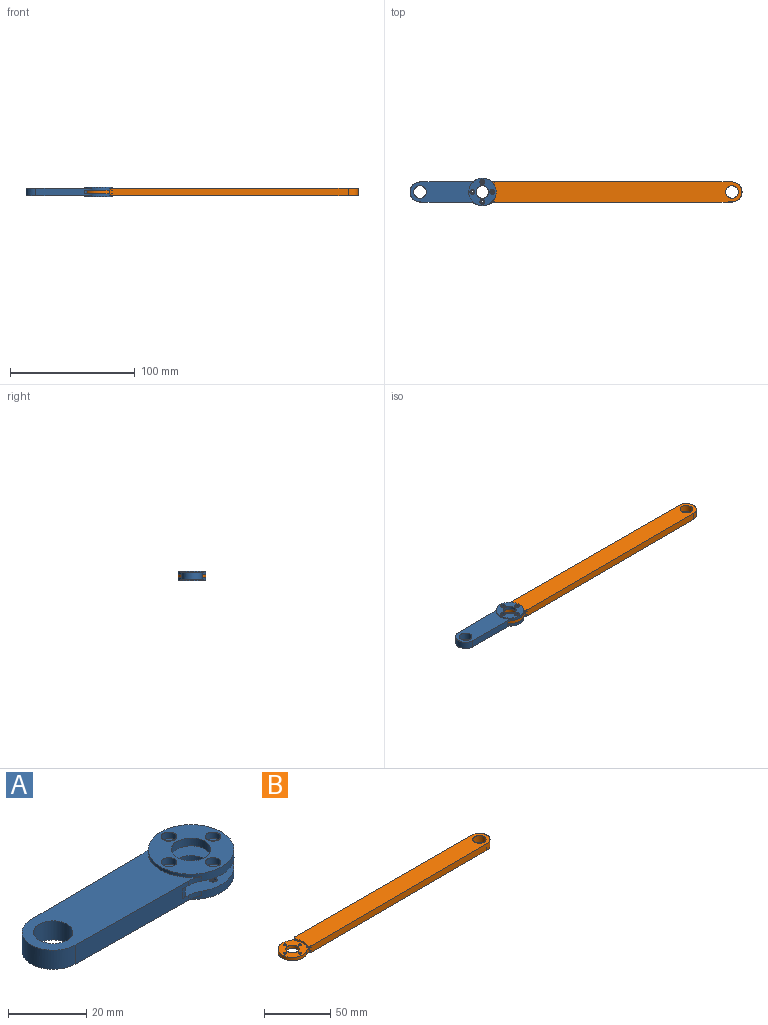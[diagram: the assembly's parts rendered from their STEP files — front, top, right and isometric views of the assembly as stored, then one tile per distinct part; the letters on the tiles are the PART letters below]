
ASSEMBLY  parts=2 mates=1
PART A: 65 faces, bbox 69x22.1x8 mm
  f0: cylinder r=2mm len=4mm, axis (0,0,1), area 25.1mm2, adj f8,f12
  f1: cylinder r=2mm len=4mm, axis (0,0,1), area 25.1mm2, adj f9,f12
  f2: cylinder r=2mm len=4mm, axis (0,0,1), area 25.1mm2, adj f10,f12
  f3: cylinder r=2mm len=4mm, axis (0,0,1), area 25.1mm2, adj f11,f12
  f4: plane 4.62x4mm, normal (0,0,-1), area 10.7mm2, adj f19,f20,f21,f22,f23,f24,f38
  f5: plane 4.62x4mm, normal (0,0,-1), area 10.7mm2, adj f13,f14,f15,f16,f17,f18,f39
  f6: plane 4.62x4mm, normal (0,0,-1), area 10.7mm2, adj f25,f26,f27,f28,f29,f30,f40
  f7: plane 4.62x4mm, normal (0,0,-1), area 10.7mm2, adj f31,f32,f33,f34,f35,f36,f41
  f8: plane 4.02x4mm, normal (0,0,1), area 9.4mm2, adj f0,f43
  f9: plane 4.02x4mm, normal (0,0,1), area 9.4mm2, adj f1,f44
  f10: plane 4.02x4mm, normal (0,0,1), area 9.4mm2, adj f2,f45
  f11: plane 4.02x4mm, normal (0,0,1), area 9.4mm2, adj f3,f46
  f12: plane 22.06x22mm, normal (0,0,1), area 249.7mm2, adj f0,f1,f2,f3,f42,f48
  f13: plane 2.31x1.7mm, normal (0,-1,0), area 3.9mm2, adj f5,f14,f18,f51
  f14: plane 2x1.7mm, normal (-0.87,-0.5,0), area 3.9mm2, adj f5,f13,f15,f51
  f15: plane 2x1.7mm, normal (-0.87,0.5,0), area 3.9mm2, adj f5,f14,f16,f51
  f16: plane 2.31x1.7mm, normal (0,1,0), area 3.9mm2, adj f5,f15,f17,f51
  f17: plane 2x1.7mm, normal (0.87,0.5,0), area 3.9mm2, adj f5,f16,f18,f51
  f18: plane 2x1.7mm, normal (0.87,-0.5,0), area 3.9mm2, adj f5,f13,f17,f51
  f19: plane 2.31x1.7mm, normal (0,-1,0), area 3.9mm2, adj f4,f20,f24,f51
  f20: plane 2x1.7mm, normal (-0.87,-0.5,0), area 3.9mm2, adj f4,f19,f21,f51
  f21: plane 2x1.7mm, normal (-0.87,0.5,0), area 3.9mm2, adj f4,f20,f22,f51
  f22: plane 2.31x1.7mm, normal (0,1,0), area 3.9mm2, adj f4,f21,f23,f51
  f23: plane 2x1.7mm, normal (0.87,0.5,0), area 3.9mm2, adj f4,f22,f24,f51
  f24: plane 2x1.7mm, normal (0.87,-0.5,0), area 3.9mm2, adj f4,f19,f23,f51
  f25: plane 2.31x1.7mm, normal (0,-1,0), area 3.9mm2, adj f6,f26,f30,f51
  f26: plane 2x1.7mm, normal (-0.87,-0.5,0), area 3.9mm2, adj f6,f25,f27,f51
  f27: plane 2x1.7mm, normal (-0.87,0.5,0), area 3.9mm2, adj f6,f26,f28,f51
  f28: plane 2.31x1.7mm, normal (0,1,0), area 3.9mm2, adj f6,f27,f29,f51
  f29: plane 2x1.7mm, normal (0.87,0.5,0), area 3.9mm2, adj f6,f28,f30,f51
  f30: plane 2x1.7mm, normal (0.87,-0.5,0), area 3.9mm2, adj f6,f25,f29,f51
  f31: plane 2.31x1.7mm, normal (0,-1,0), area 3.9mm2, adj f7,f32,f36,f51
  f32: plane 2x1.7mm, normal (-0.87,-0.5,0), area 3.9mm2, adj f7,f31,f33,f51
  f33: plane 2x1.7mm, normal (-0.87,0.5,0), area 3.9mm2, adj f7,f32,f34,f51
  f34: plane 2.31x1.7mm, normal (0,1,0), area 3.9mm2, adj f7,f33,f35,f51
  f35: plane 2x1.7mm, normal (0.87,0.5,0), area 3.9mm2, adj f7,f34,f36,f51
  f36: plane 2x1.7mm, normal (0.87,-0.5,0), area 3.9mm2, adj f7,f31,f35,f51
  f37: cylinder r=5.05mm len=10.1mm, axis (0,0,1), area 77.7mm2, adj f51,f52
  f38: cylinder r=1mm len=2mm, axis (0,0,1), area 4.7mm2, adj f4,f52
  f39: cylinder r=1mm len=2mm, axis (0,0,1), area 4.7mm2, adj f5,f52
  f40: cylinder r=1mm len=2mm, axis (0,0,1), area 4.7mm2, adj f6,f52
  f41: cylinder r=1mm len=2mm, axis (0,0,1), area 4.7mm2, adj f7,f52
  f42: cylinder r=5.05mm len=10.1mm, axis (0,0,1), area 77.7mm2, adj f12,f54
  f43: cylinder r=1mm len=2mm, axis (0,0,1), area 2.8mm2, adj f8,f54
  f44: cylinder r=1mm len=2mm, axis (0,0,1), area 2.8mm2, adj f9,f54
  f45: cylinder r=1mm len=2mm, axis (0,0,1), area 2.8mm2, adj f10,f54
  f46: cylinder r=1mm len=2mm, axis (0,0,1), area 2.8mm2, adj f11,f54
  f47: cylinder r=11.07mm len=10.82mm, axis (0,0,1), area 35mm2, adj f50,f52,f54,f55
  f48: cylinder r=11mm len=22mm, axis (0,0,1), area 136.1mm2, adj f12,f49,f53,f54,f56
  f49: cylinder r=8mm len=3.96mm, axis (0,0,1), area 6mm2, adj f48,f54,f56,f57
  f50: cylinder r=2mm len=3.1mm, axis (0,0,1), area 13mm2, adj f47,f52,f54,f57
  f51: plane 22.06x22mm, normal (0,0,-1), area 244.6mm2, adj f13,f14,f15,f16,f17,f18,f19,f20
  f52: plane 22.44x22.05mm, normal (0,0,1), area 296.8mm2, adj f37,f38,f39,f40,f41,f47,f50,f55
  f53: cylinder r=8mm len=3.96mm, axis (0,0,1), area 6mm2, adj f48,f54,f56,f61
  f54: plane 22.44x22.05mm, normal (0,0,-1), area 296.8mm2, adj f42,f43,f44,f45,f46,f47,f48,f49
  f55: cylinder r=2mm len=3.1mm, axis (0,0,-1), area 13mm2, adj f47,f52,f54,f61
  f56: plane 52.48x19mm, normal (0,0,1), area 680.7mm2, adj f48,f49,f53,f57,f61,f62,f63
  f57: plane 40.57x6mm, normal (-0.01,-1,0), area 237.5mm2, adj f49,f50,f52,f54,f56,f58,f62,f64
  f58: cylinder r=8mm len=3.96mm, axis (0,0,1), area 6mm2, adj f52,f57,f59,f64
  f59: cylinder r=11mm len=22mm, axis (0,0,1), area 136.1mm2, adj f51,f52,f58,f60,f64
  f60: cylinder r=8mm len=3.96mm, axis (0,0,1), area 6mm2, adj f52,f59,f61,f64
  f61: plane 40.57x6mm, normal (-0.01,1,0), area 237.5mm2, adj f52,f53,f54,f55,f56,f60,f62,f64
  f62: cylinder r=8mm len=16mm, axis (0,0,1), area 149.8mm2, adj f56,f57,f61,f64
  f63: cylinder r=5.05mm len=10.1mm, axis (0,0,1), area 190.4mm2, adj f56,f64
  f64: plane 52.48x19mm, normal (0,0,-1), area 680.7mm2, adj f57,f58,f59,f60,f61,f62,f63
PART B: 22 faces, bbox 219.1x22x6 mm
  f0: cylinder r=11mm len=22mm, axis (0,0,1), area 138.1mm2, adj f7,f9,f10,f12
  f1: cylinder r=5.05mm len=10.1mm, axis (0,0,1), area 95.2mm2, adj f10,f12
  f2: cylinder r=1mm len=3mm, axis (0,0,1), area 18.8mm2, adj f10,f12
  f3: cylinder r=1mm len=3mm, axis (0,0,1), area 18.8mm2, adj f10,f12
  f4: cylinder r=1mm len=3mm, axis (0,0,1), area 18.8mm2, adj f10,f12
  f5: cylinder r=1mm len=3mm, axis (0,0,1), area 18.8mm2, adj f10,f12
  f6: cylinder r=11.07mm len=10.96mm, axis (0,0,1), area 17.2mm2, adj f8,f10,f11,f13
  f7: cylinder r=8mm len=3.96mm, axis (0,0,-1), area 12.5mm2, adj f0,f10,f12,f15
  f8: cylinder r=2mm len=2.99mm, axis (0,0,-1), area 6.3mm2, adj f6,f10,f13,f15
  f9: cylinder r=8mm len=3.96mm, axis (0,0,-1), area 12.5mm2, adj f0,f10,f12,f17
  f10: plane 22.41x22.05mm, normal (0,0,1), area 296.8mm2, adj f0,f1,f2,f3,f4,f5,f6,f7
  f11: cylinder r=2mm len=2.99mm, axis (0,0,1), area 6.3mm2, adj f6,f10,f13,f17
  f12: plane 22.41x22.05mm, normal (0,0,-1), area 296.8mm2, adj f0,f1,f2,f3,f4,f5,f7,f9
  f13: plane 198.7x16.95mm, normal (0,0,1), area 3146mm2, adj f6,f8,f11,f15,f16,f17,f20
  f14: cylinder r=2mm len=2.99mm, axis (0,0,-1), area 6.3mm2, adj f12,f15,f19,f21
  f15: plane 190.58x6mm, normal (0,-1,0), area 1137.7mm2, adj f7,f8,f10,f12,f13,f14,f16,f21
  f16: cylinder r=8mm len=16mm, axis (0,0,1), area 150.6mm2, adj f13,f15,f17,f21
  f17: plane 190.58x6mm, normal (0,1,0), area 1137.7mm2, adj f9,f10,f11,f12,f13,f16,f18,f21
  f18: cylinder r=2mm len=2.99mm, axis (0,0,1), area 6.3mm2, adj f12,f17,f19,f21
  f19: cylinder r=11.07mm len=10.96mm, axis (0,0,1), area 17.2mm2, adj f12,f14,f18,f21
  f20: cylinder r=5.05mm len=10.1mm, axis (0,0,1), area 190.4mm2, adj f13,f21
  f21: plane 198.7x16.95mm, normal (0,0,-1), area 3146mm2, adj f14,f15,f16,f17,f18,f19,f20
PLACE A at identity
PLACE B t=(-0.28,0,0.05)mm
MATE fastened B.f10 <-> A.f37  axis (0,0,1) through (0,0,1.55)mm
